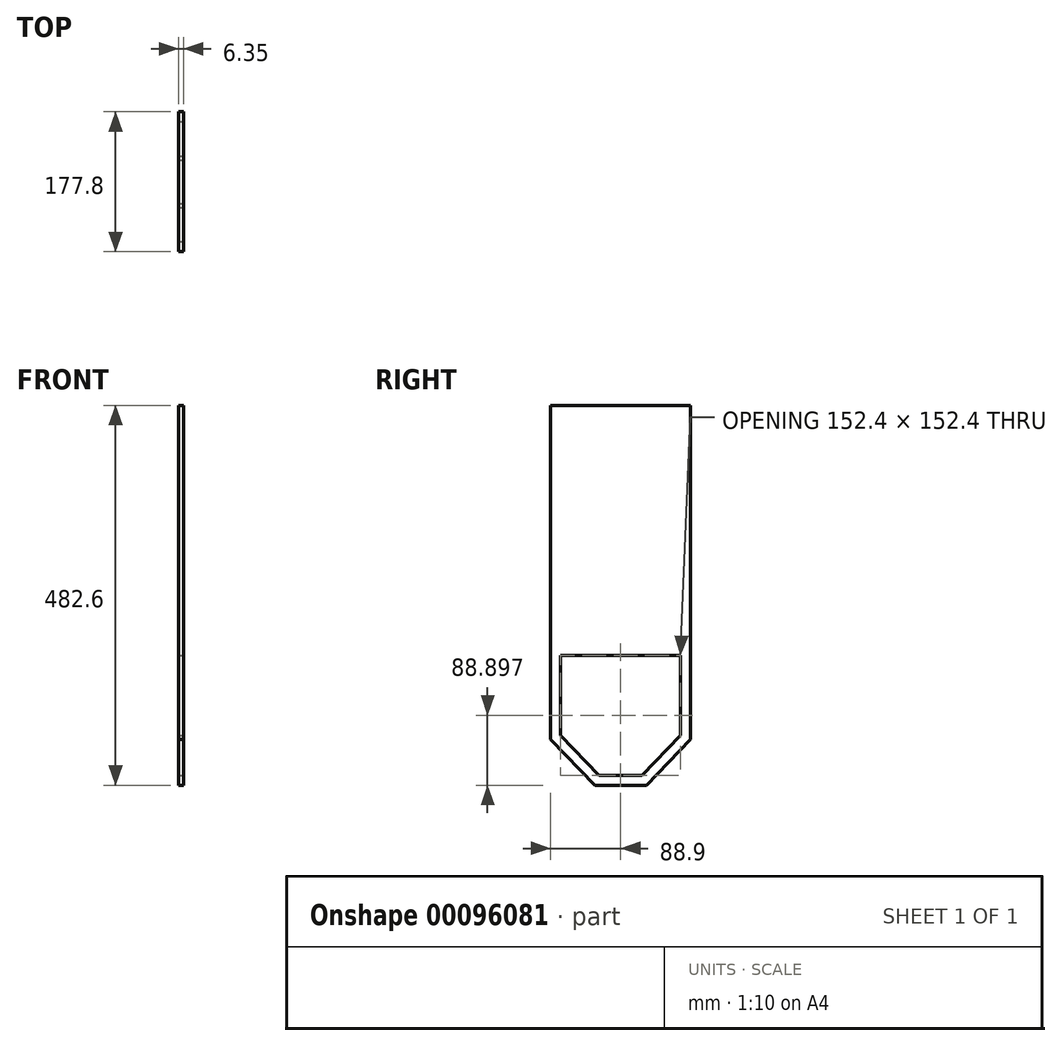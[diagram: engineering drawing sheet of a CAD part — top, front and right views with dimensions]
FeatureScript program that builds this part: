
annotation { "Feature Type Name" : "Feature", "Feature Type Description" : "" }
export const myFeature = defineFeature(function(context is Context, id is Id, definition is map)
    precondition{}
    {
        {
            var Q0;
            Q0=qCreatedBy(makeId("Right.planeOp"),FACE);
            var sketch = newSketch(context, id + "F0", { "sketchPlane" : qUnion([Q0])});
            skLineSegment(sketch, "E0.top", {"start": v(88.9, 212.1) * mm, "end": v(-88.9, 212.1) * mm});
            skLineSegment(sketch, "E0.left", {"start": v(88.9, -212.1) * mm, "end": v(88.9, 212.1) * mm});
            skLineSegment(sketch, "E0.right", {"start": v(-88.9, -212.1) * mm, "end": v(-88.9, 212.1) * mm});
            skPoint(sketch, "E0.middle", {"position": v(0, 0) * mm});
            skLineSegment(sketch, "E1", {"start": v(-88.9, -212.1) * mm, "end": v(-32.8, -270.5) * mm});
            skLineSegment(sketch, "E2", {"start": v(-32.8, -270.5) * mm, "end": v(32.8, -270.5) * mm});
            skLineSegment(sketch, "E3", {"start": v(32.8, -270.5) * mm, "end": v(88.9, -212.1) * mm});
            skLineSegment(sketch, "E4", {"start": v(-76.2, -105.4) * mm, "end": v(-76.2, -207) * mm});
            skLineSegment(sketch, "E5", {"start": v(-76.2, -207) * mm, "end": v(-27.38, -257.8) * mm});
            skLineSegment(sketch, "E6", {"start": v(-27.38, -257.8) * mm, "end": v(27.38, -257.8) * mm});
            skLineSegment(sketch, "E7", {"start": v(27.38, -257.8) * mm, "end": v(76.2, -207) * mm});
            skLineSegment(sketch, "E8", {"start": v(76.2, -207) * mm, "end": v(76.2, -105.4) * mm});
            skLineSegment(sketch, "E9", {"start": v(76.2, -105.4) * mm, "end": v(-76.2, -105.4) * mm});
            skLineSegment(sketch, "E10", {"start": v(0, 0) * mm, "end": v(0, -257.8) * mm, "construction": true});
            skLineSegment(sketch, "E11", {"start": v(0, -257.8) * mm, "end": v(0, -181.6) * mm, "construction": true});
            skPoint(sketch, "E12", {"position": v(0, -181.6) * mm});
            skLineSegment(sketch, "E13", {"start": v(-47.34, -181.6) * mm, "end": v(44.2, -181.6) * mm});
            skLineSegment(sketch, "E14", {"start": v(0, -153.19) * mm, "end": v(0, -158.27) * mm});
            skSolve(sketch);
        }
        {
            var Q0;
            Q0=makeQuery(id+"F0.imprint","IMPRINT",FACE,{"disambiguationData":[TD([[makeQuery(id+"F0.imprint","IMPRINT",EDGE,{"derivedFrom":sQuery(id+"F0.wireOp",EDGE,"E0.top")}),1.0]])]});
            extrude(context, id + "F1", {"entities" : qUnion([Q0]), "oppositeDirection" : true, "depth" : 6.35 * mm});
        }
    });
